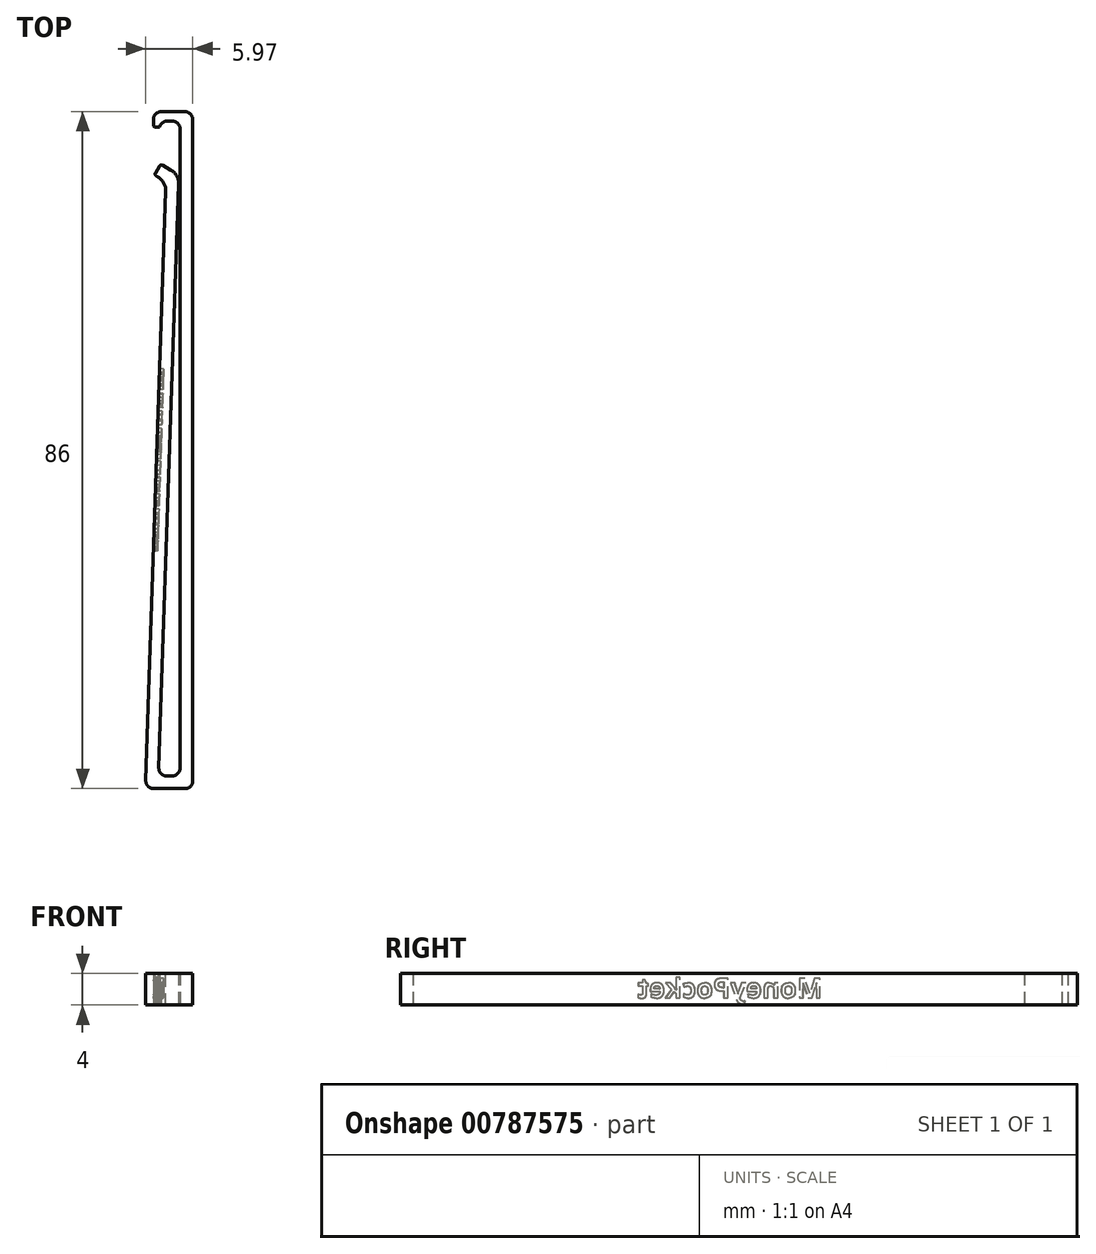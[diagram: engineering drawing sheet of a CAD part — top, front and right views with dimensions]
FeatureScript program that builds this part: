
annotation { "Feature Type Name" : "Feature", "Feature Type Description" : "" }
export const myFeature = defineFeature(function(context is Context, id is Id, definition is map)
    precondition{}
    {
        {
            var Q0;
            Q0=qCreatedBy(makeId("Top.planeOp"),FACE);
            var sketch = newSketch(context, id + "F0", { "sketchPlane" : qUnion([Q0])});
            skLineSegment(sketch, "E0", {"start": v(0, 0) * mm, "end": v(6, 0) * mm});
            skLineSegment(sketch, "E1", {"start": v(6, 0) * mm, "end": v(6, 86) * mm});
            skLineSegment(sketch, "E2", {"start": v(6, 86) * mm, "end": v(1, 86) * mm});
            skLineSegment(sketch, "E3", {"start": v(1, 86) * mm, "end": v(1, 84) * mm});
            skLineSegment(sketch, "E4", {"start": v(1, 84) * mm, "end": v(1.8, 84) * mm});
            skLineSegment(sketch, "E5", {"start": v(1.8, 84) * mm, "end": v(1.8, 84.8) * mm});
            skLineSegment(sketch, "E6", {"start": v(1.8, 84.8) * mm, "end": v(4.4, 84.8) * mm});
            skLineSegment(sketch, "E7", {"start": v(4.4, 84.8) * mm, "end": v(4.4, 1.6) * mm});
            skLineSegment(sketch, "E8", {"start": v(4.4, 1.6) * mm, "end": v(1.66, 1.6) * mm});
            skLineSegment(sketch, "E9", {"start": v(1.6, -0.03) * mm, "end": v(1.6, 0) * mm});
            skLineSegment(sketch, "E10", {"start": v(0, 0) * mm, "end": v(2.62, 77.1) * mm});
            skLineSegment(sketch, "E11", {"start": v(4.25, 78) * mm, "end": v(1.92, 79.34) * mm});
            skLineSegment(sketch, "E12", {"start": v(2.62, 77.1) * mm, "end": v(1.12, 77.96) * mm});
            skLineSegment(sketch, "E13", {"start": v(1.92, 79.34) * mm, "end": v(1.12, 77.96) * mm});
            skPoint(sketch, "E13.endSnap0", {"position": v(1.56, 77.7) * mm});
            skPoint(sketch, "E14.orphan", {"position": v(1.56, 78.71) * mm});
            skPoint(sketch, "E15.orphan", {"position": v(-147.46, 163.74) * mm});
            skLineSegment(sketch, "E16.trimOffspring", {"start": v(1.66, 1.6) * mm, "end": v(4.25, 78) * mm});
            skPoint(sketch, "E17.trimOffspring.end.orphan", {"position": v(0, 0.8) * mm});
            skPoint(sketch, "E18.orphan", {"position": v(2.65, 78) * mm});
            skPoint(sketch, "E19.orphan", {"position": v(150.57, -8.33) * mm});
            skSolve(sketch);
        }
        {
            var Q0;
            {var subQ3=sQuery(id+"F0.wireOp",EDGE,"E1");Q0=makeQuery(id+"F0.imprint","IMPRINT",FACE,{"disambiguationData":[TD([[makeQuery(id+"F0.imprint","IMPRINT",EDGE,{"derivedFrom":subQ3}),1.0]])]});}
            extrude(context, id + "F1", {"entities" : qUnion([Q0]), "depth" : 4 * mm, "offsetDistance" : 25 * mm});
        }
        {
            var Q0;
            Q0=makeQuery(id+"F1.opExtrude","SWEPT_EDGE",EDGE,{"disambiguationData":[OSD([sQuery(id+"F0.wireOp",EDGE,"E11"),sQuery(id+"F0.wireOp",EDGE,"E16.trimOffspring")])]});
            var Q1;
            Q1=makeQuery(id+"F1.opExtrude","SWEPT_EDGE",EDGE,{"disambiguationData":[OSD([sQuery(id+"F0.wireOp",EDGE,"E10"),sQuery(id+"F0.wireOp",EDGE,"E12")])]});
            fillet(context, id + "F2", {"entities" : qUnion([Q0, Q1]), "radius" : 2 * mm, "tangentPropagation" : true, "allowEdgeOverflow" : false});
        }
        {
            var Q0;
            Q0=makeQuery(id+"F1.opExtrude","SWEPT_EDGE",EDGE,{"disambiguationData":[OSD([sQuery(id+"F0.wireOp",EDGE,"E5"),sQuery(id+"F0.wireOp",EDGE,"E6")])]});
            var Q1;
            Q1=makeQuery(id+"F1.opExtrude","SWEPT_EDGE",EDGE,{"disambiguationData":[OSD([sQuery(id+"F0.wireOp",EDGE,"E2"),sQuery(id+"F0.wireOp",EDGE,"E3")])]});
            var Q2;
            Q2=makeQuery(id+"F1.opExtrude","SWEPT_EDGE",EDGE,{"disambiguationData":[OSD([sQuery(id+"F0.wireOp",EDGE,"E6"),sQuery(id+"F0.wireOp",EDGE,"E7")])]});
            var Q3;
            Q3=makeQuery(id+"F1.opExtrude","SWEPT_EDGE",EDGE,{"disambiguationData":[OSD([sQuery(id+"F0.wireOp",EDGE,"E1"),sQuery(id+"F0.wireOp",EDGE,"E2")])]});
            var Q4;
            Q4=makeQuery(id+"F1.opExtrude","SWEPT_EDGE",EDGE,{"disambiguationData":[OSD([sQuery(id+"F0.wireOp",EDGE,"E0"),sQuery(id+"F0.wireOp",EDGE,"E10")])]});
            var Q5;
            Q5=makeQuery(id+"F1.opExtrude","SWEPT_EDGE",EDGE,{"disambiguationData":[OSD([sQuery(id+"F0.wireOp",EDGE,"E0"),sQuery(id+"F0.wireOp",EDGE,"E1")])]});
            var Q6;
            Q6=makeQuery(id+"F1.opExtrude","SWEPT_EDGE",EDGE,{"disambiguationData":[OSD([sQuery(id+"F0.wireOp",EDGE,"E7"),sQuery(id+"F0.wireOp",EDGE,"E8")])]});
            var Q7;
            Q7=makeQuery(id+"F1.opExtrude","SWEPT_EDGE",EDGE,{"disambiguationData":[OSD([sQuery(id+"F0.wireOp",EDGE,"E8"),sQuery(id+"F0.wireOp",EDGE,"E16.trimOffspring")])]});
            fillet(context, id + "F3", {"entities" : qUnion([Q0, Q1, Q2, Q3, Q4, Q5, Q6, Q7]), "radius" : 1 * mm, "tangentPropagation" : true, "allowEdgeOverflow" : false});
        }
        {
            var Q0;
            Q0=makeQuery(id+"F1.opExtrude","SWEPT_EDGE",EDGE,{"disambiguationData":[OSD([sQuery(id+"F0.wireOp",EDGE,"E11"),sQuery(id+"F0.wireOp",EDGE,"E13")])]});
            var Q1;
            Q1=makeQuery(id+"F1.opExtrude","SWEPT_EDGE",EDGE,{"disambiguationData":[OSD([sQuery(id+"F0.wireOp",EDGE,"E12"),sQuery(id+"F0.wireOp",EDGE,"E13")])]});
            var Q2;
            Q2=makeQuery(id+"F1.opExtrude","SWEPT_EDGE",EDGE,{"disambiguationData":[OSD([sQuery(id+"F0.wireOp",EDGE,"E3"),sQuery(id+"F0.wireOp",EDGE,"E4")])]});
            var Q3;
            Q3=makeQuery(id+"F1.opExtrude","SWEPT_EDGE",EDGE,{"disambiguationData":[OSD([sQuery(id+"F0.wireOp",EDGE,"E4"),sQuery(id+"F0.wireOp",EDGE,"E5")])]});
            fillet(context, id + "F4", {"entities" : qUnion([Q0, Q1, Q2, Q3]), "radius" : 0.3 * mm, "tangentPropagation" : true, "allowEdgeOverflow" : false});
        }
        {
            var Q0;
            Q0=makeQuery(id+"F1.opExtrude","SWEPT_FACE",FACE,{"disambiguationData":[OSD([sQuery(id+"F0.wireOp",EDGE,"E10")])]});
            var sketch = newSketch(context, id + "F5", { "sketchPlane" : qUnion([Q0])});
            skText(sketch, "E20", { "text": "MoneyPocket", "fontName": "OpenSans-Bold.ttf"});
            const initialGuessF5  = {"E20": [-0.05367, 0.0009, 1, 0, 0.0025]};
            skSetInitialGuess(sketch, initialGuessF5);
            skSolve(sketch);
        }
        {
            var Q0;
            Q0 = qSketchRegion(id + "F5", true);
            extrude(context, id + "F6", {"entities" : qUnion([Q0]), "operationType" : NewBodyOperationType.REMOVE, "oppositeDirection" : true, "depth" : 0.5 * mm, "offsetDistance" : 25 * mm});
        }
    });
